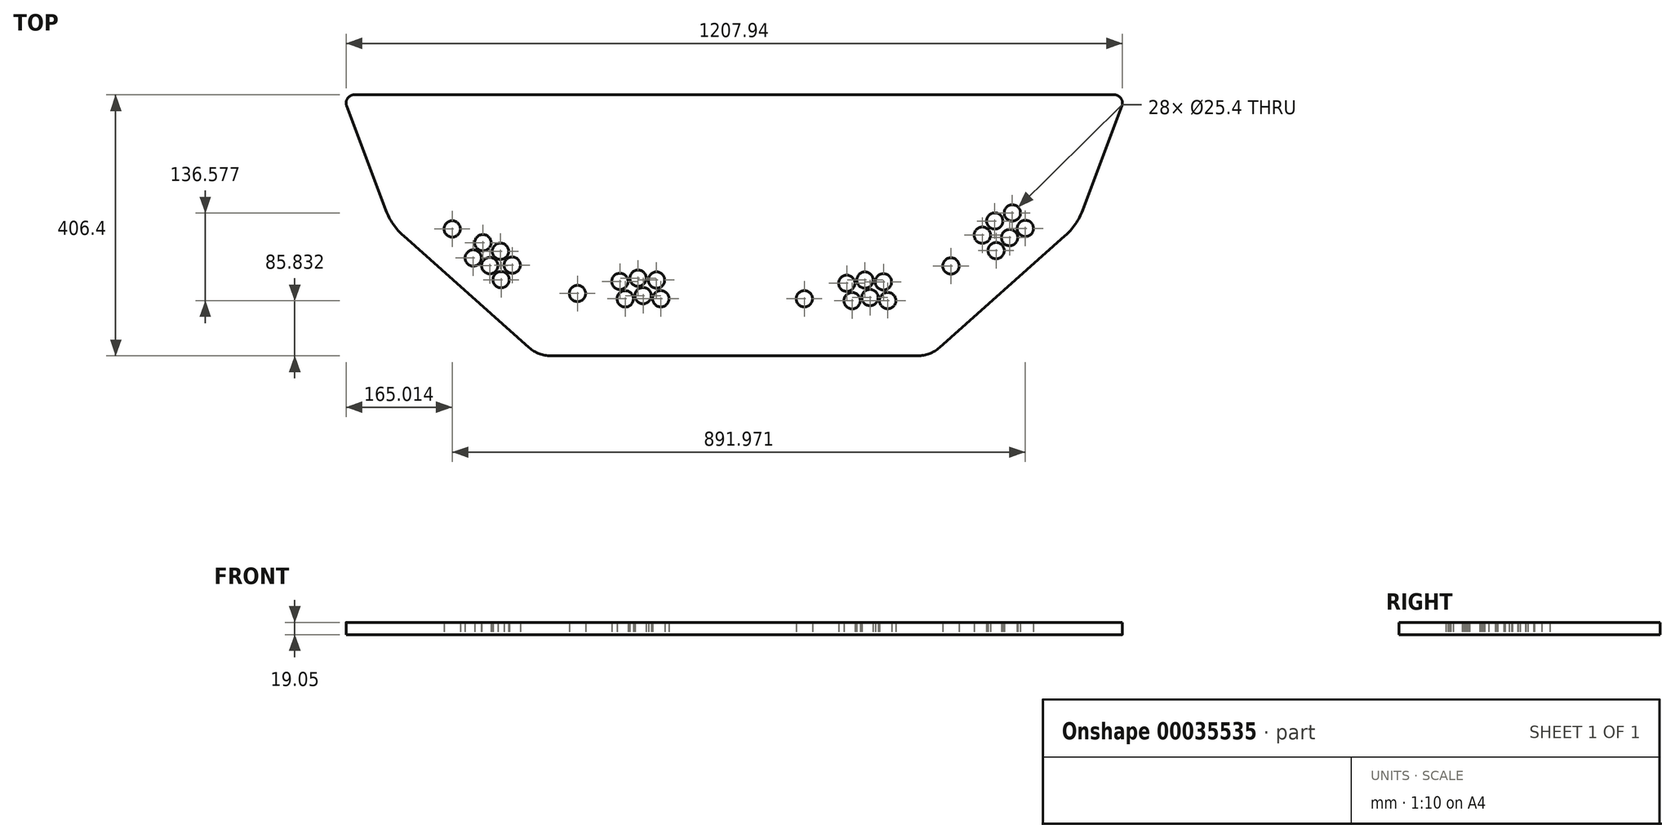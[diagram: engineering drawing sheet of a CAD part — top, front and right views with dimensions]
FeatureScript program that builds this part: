
annotation { "Feature Type Name" : "Feature", "Feature Type Description" : "" }
export const myFeature = defineFeature(function(context is Context, id is Id, definition is map)
    precondition{}
    {
        {
            var Q0;
            Q0=qCreatedBy(makeId("Top.planeOp"),FACE);
            var sketch = newSketch(context, id + "F0", { "sketchPlane" : qUnion([Q0])});
            skLineSegment(sketch, "E0", {"start": v(-285.49, -203.2) * mm, "end": v(0, -203.2) * mm});
            skLineSegment(sketch, "E1", {"start": v(0, -203.2) * mm, "end": v(285.49, -203.2) * mm});
            skLineSegment(sketch, "E2", {"start": v(319.24, -190.37) * mm, "end": v(514.6, -16.71) * mm});
            skLineSegment(sketch, "E3", {"start": v(542.23, 23.55) * mm, "end": v(603.17, 186.04) * mm});
            skLineSegment(sketch, "E4", {"start": v(591.27, 203.2) * mm, "end": v(0, 203.2) * mm});
            skLineSegment(sketch, "E5.MirrorCS", {"start": v(-591.27, 203.2) * mm, "end": v(0, 203.2) * mm});
            skLineSegment(sketch, "E6.MirrorCS", {"start": v(-542.23, 23.55) * mm, "end": v(-603.17, 186.04) * mm});
            skLineSegment(sketch, "E7.MirrorCS", {"start": v(-319.24, -190.37) * mm, "end": v(-514.6, -16.71) * mm});
            skPoint(sketch, "E8.visualSharp", {"position": v(-609.6, 203.2) * mm});
            skArc(sketch, "E8.filletArc", {"start": v(-591.27, 203.2) * mm, "mid": v(-601.71, 197.73) * mm, "end": v(-603.17, 186.04) * mm});
            skPoint(sketch, "E9.visualSharp", {"position": v(609.6, 203.2) * mm});
            skArc(sketch, "E9.filletArc", {"start": v(603.17, 186.04) * mm, "mid": v(601.71, 197.73) * mm, "end": v(591.27, 203.2) * mm});
            skPoint(sketch, "E10.visualSharp", {"position": v(-304.8, -203.2) * mm});
            skArc(sketch, "E10.filletArc", {"start": v(-319.24, -190.37) * mm, "mid": v(-303.54, -199.88) * mm, "end": v(-285.49, -203.2) * mm});
            skPoint(sketch, "E11.visualSharp", {"position": v(304.8, -203.2) * mm});
            skArc(sketch, "E11.filletArc", {"start": v(285.49, -203.2) * mm, "mid": v(303.54, -199.88) * mm, "end": v(319.24, -190.37) * mm});
            skPoint(sketch, "E12.visualSharp", {"position": v(-533.4, 0) * mm});
            skArc(sketch, "E12.filletArc", {"start": v(-542.23, 23.55) * mm, "mid": v(-530.87, 1.74) * mm, "end": v(-514.6, -16.71) * mm});
            skPoint(sketch, "E13.visualSharp", {"position": v(533.4, 0) * mm});
            skArc(sketch, "E13.filletArc", {"start": v(514.6, -16.71) * mm, "mid": v(530.87, 1.74) * mm, "end": v(542.23, 23.55) * mm});
            skCircle(sketch, "E14", {"center": v(-114.3, -114.3) * mm, "radius": 12.7 * mm});
            skCircle(sketch, "E15", {"center": v(-141.88, -109.52) * mm, "radius": 12.7 * mm});
            skCircle(sketch, "E16", {"center": v(-169.62, -114.5) * mm, "radius": 12.7 * mm});
            skCircle(sketch, "E17", {"center": v(-120.95, -85.25) * mm, "radius": 12.7 * mm});
            skCircle(sketch, "E18", {"center": v(-149.74, -82.38) * mm, "radius": 12.7 * mm});
            skCircle(sketch, "E19", {"center": v(-178.04, -87.4) * mm, "radius": 12.7 * mm});
            skCircle(sketch, "E20", {"center": v(-243.98, -106.2) * mm, "radius": 12.7 * mm});
            skCircle(sketch, "E21", {"center": v(211.17, -112.4) * mm, "radius": 12.7 * mm});
            skCircle(sketch, "E22", {"center": v(232.1, -88.13) * mm, "radius": 12.7 * mm});
            skCircle(sketch, "E23", {"center": v(183.43, -117.37) * mm, "radius": 12.7 * mm});
            skCircle(sketch, "E24", {"center": v(109.07, -114.3) * mm, "radius": 12.7 * mm});
            skCircle(sketch, "E25", {"center": v(238.75, -117.17) * mm, "radius": 12.7 * mm});
            skCircle(sketch, "E26", {"center": v(175, -90.27) * mm, "radius": 12.7 * mm});
            skCircle(sketch, "E27", {"center": v(203.3, -85.25) * mm, "radius": 12.7 * mm});
            skCircle(sketch, "E28", {"center": v(407.53, -39.48) * mm, "radius": 12.7 * mm});
            skCircle(sketch, "E29", {"center": v(405.35, 6.7) * mm, "radius": 12.7 * mm});
            skCircle(sketch, "E30", {"center": v(432.72, 19.2) * mm, "radius": 12.7 * mm});
            skCircle(sketch, "E31", {"center": v(453.01, -4.85) * mm, "radius": 12.7 * mm});
            skCircle(sketch, "E32", {"center": v(386.06, -15.43) * mm, "radius": 12.7 * mm});
            skCircle(sketch, "E33", {"center": v(337.2, -63.37) * mm, "radius": 12.7 * mm});
            skCircle(sketch, "E34", {"center": v(428.4, -19.07) * mm, "radius": 12.7 * mm});
            skCircle(sketch, "E35", {"center": v(-406.24, -50.88) * mm, "radius": 12.7 * mm});
            skCircle(sketch, "E36", {"center": v(-363.85, -40.45) * mm, "radius": 12.7 * mm});
            skCircle(sketch, "E37", {"center": v(-438.96, -5.68) * mm, "radius": 12.7 * mm});
            skCircle(sketch, "E38", {"center": v(-345.5, -62.06) * mm, "radius": 12.7 * mm});
            skCircle(sketch, "E39", {"center": v(-391.17, -27) * mm, "radius": 12.7 * mm});
            skCircle(sketch, "E40", {"center": v(-380.44, -62.78) * mm, "radius": 12.7 * mm});
            skCircle(sketch, "E41", {"center": v(-362.87, -84.7) * mm, "radius": 12.7 * mm});
            skSolve(sketch);
        }
        {
            var Q0;
            Q0=makeQuery(id+"F0.imprint","IMPRINT",FACE,{"disambiguationData":[TD([[makeQuery(id+"F0.imprint","IMPRINT",EDGE,{"derivedFrom":sQuery(id+"F0.wireOp",EDGE,"E0")}),1.0]])]});
            extrude(context, id + "F1", {"entities" : qUnion([Q0]), "depth" : 19.05 * mm});
        }
    });
